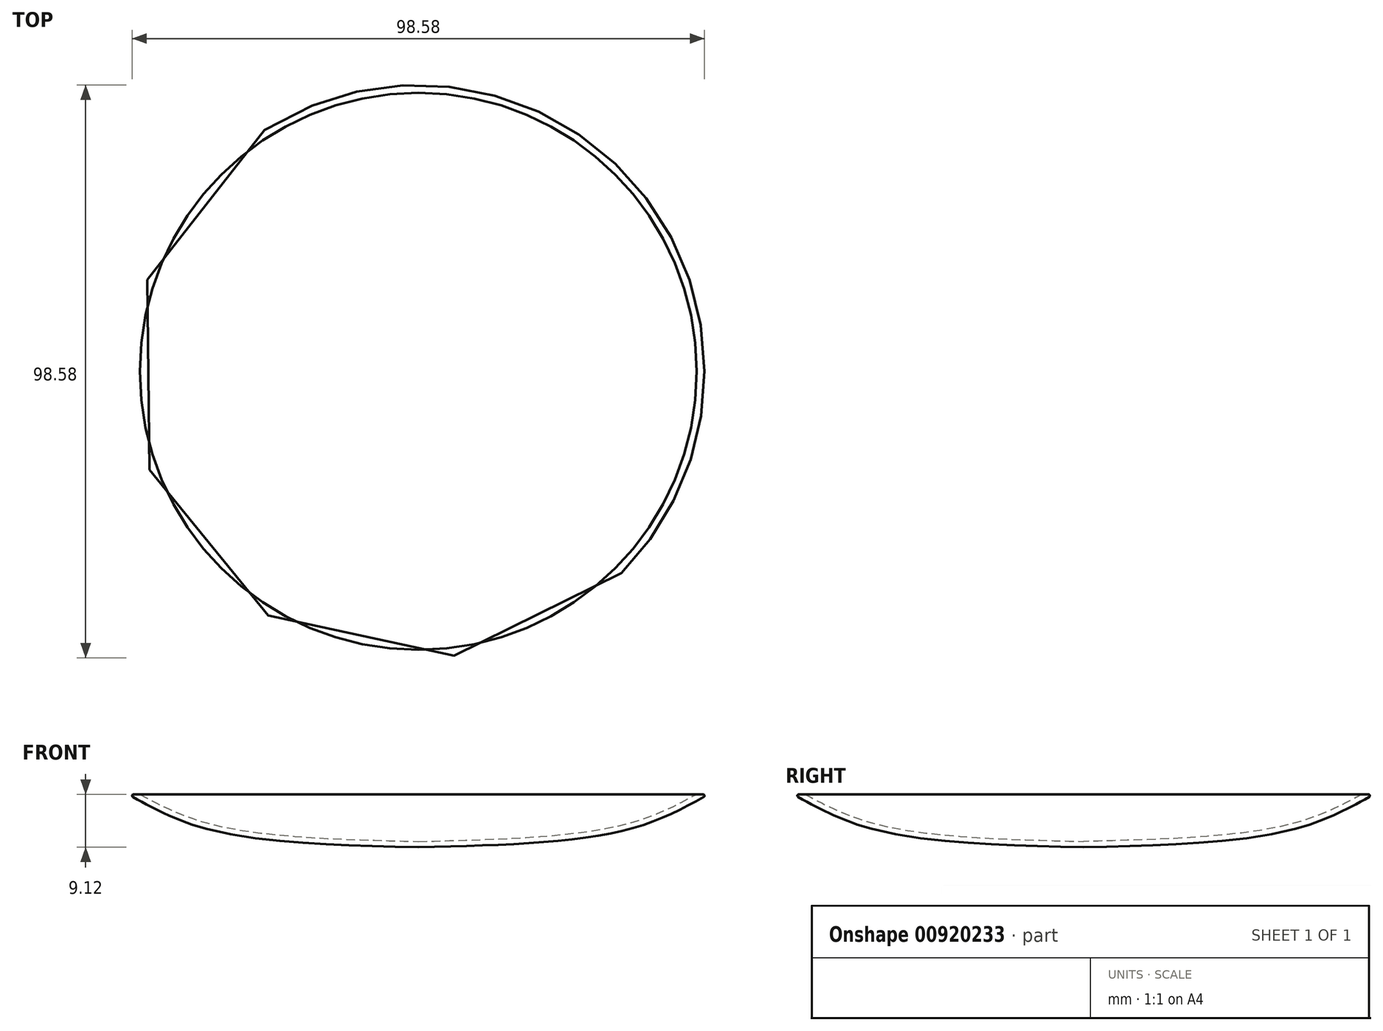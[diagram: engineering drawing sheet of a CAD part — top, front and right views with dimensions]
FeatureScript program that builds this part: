
annotation { "Feature Type Name" : "Feature", "Feature Type Description" : "" }
export const myFeature = defineFeature(function(context is Context, id is Id, definition is map)
    precondition{}
    {
        {
            var Q0;
            Q0=qCreatedBy(makeId("Front.planeOp"),FACE);
            var sketch = newSketch(context, id + "F0", { "sketchPlane" : qUnion([Q0])});
            skLineSegment(sketch, "E0", {"start": v(0, 9.12) * mm, "end": v(50, 9.12) * mm});
            skLineSegment(sketch, "E1", {"start": v(0, 9.12) * mm, "end": v(0, 0) * mm});
            skFitSpline(sketch, "E2", {"points": [v(0, 0) * mm, v(35.49, 2.9) * mm, v(50, 9.12) * mm], "startDerivative": vector(65.97, 1.61) * mm, "endDerivative": vector(31.74, 17.7) * mm});
            skSolve(sketch);
        }
        {
            var Q0;
            Q0 = qSketchRegion(id + "F0", true);
            var Q1;
            Q1=makeQuery(id+"F0.imprint","IMPRINT",FACE,{"disambiguationData":[TD([[makeQuery(id+"F0.imprint","IMPRINT",EDGE,{"derivedFrom":sQuery(id+"F0.wireOp",EDGE,"E0")}),-1.0]])]});
            var Q2;
            Q2=sQuery(id+"F0.wireOp",EDGE,"E1");
            revolve(context, id + "F1", {"surfaceOperationType" : NewSurfaceOperationType.NEW, "entities" : qUnion([Q0, Q1]), "axis" : qUnion([Q2]), "revolveType" : RevolveType.FULL});
        }
        {
            var Q0;
            Q0=makeQuery(id+"F1.opRevolve","SWEPT_FACE",FACE,{"disambiguationData":[OSD([sQuery(id+"F0.wireOp",EDGE,"E0")])]});
            shell(context, id + "F2", {"entities" : qUnion([Q0]), "thickness" : 1 * mm});
        }
        {
            var Q0;
            Q0=makeQuery(id+"F1.opRevolve","SWEPT_EDGE",EDGE,{"disambiguationData":[OSD([sQuery(id+"F0.wireOp",EDGE,"E0"),sQuery(id+"F0.wireOp",EDGE,"E2")])]});
            fillet(context, id + "F3", {"entities" : qUnion([Q0]), "radius" : .25 * mm, "tangentPropagation" : true, "allowEdgeOverflow" : false});
        }
    });
